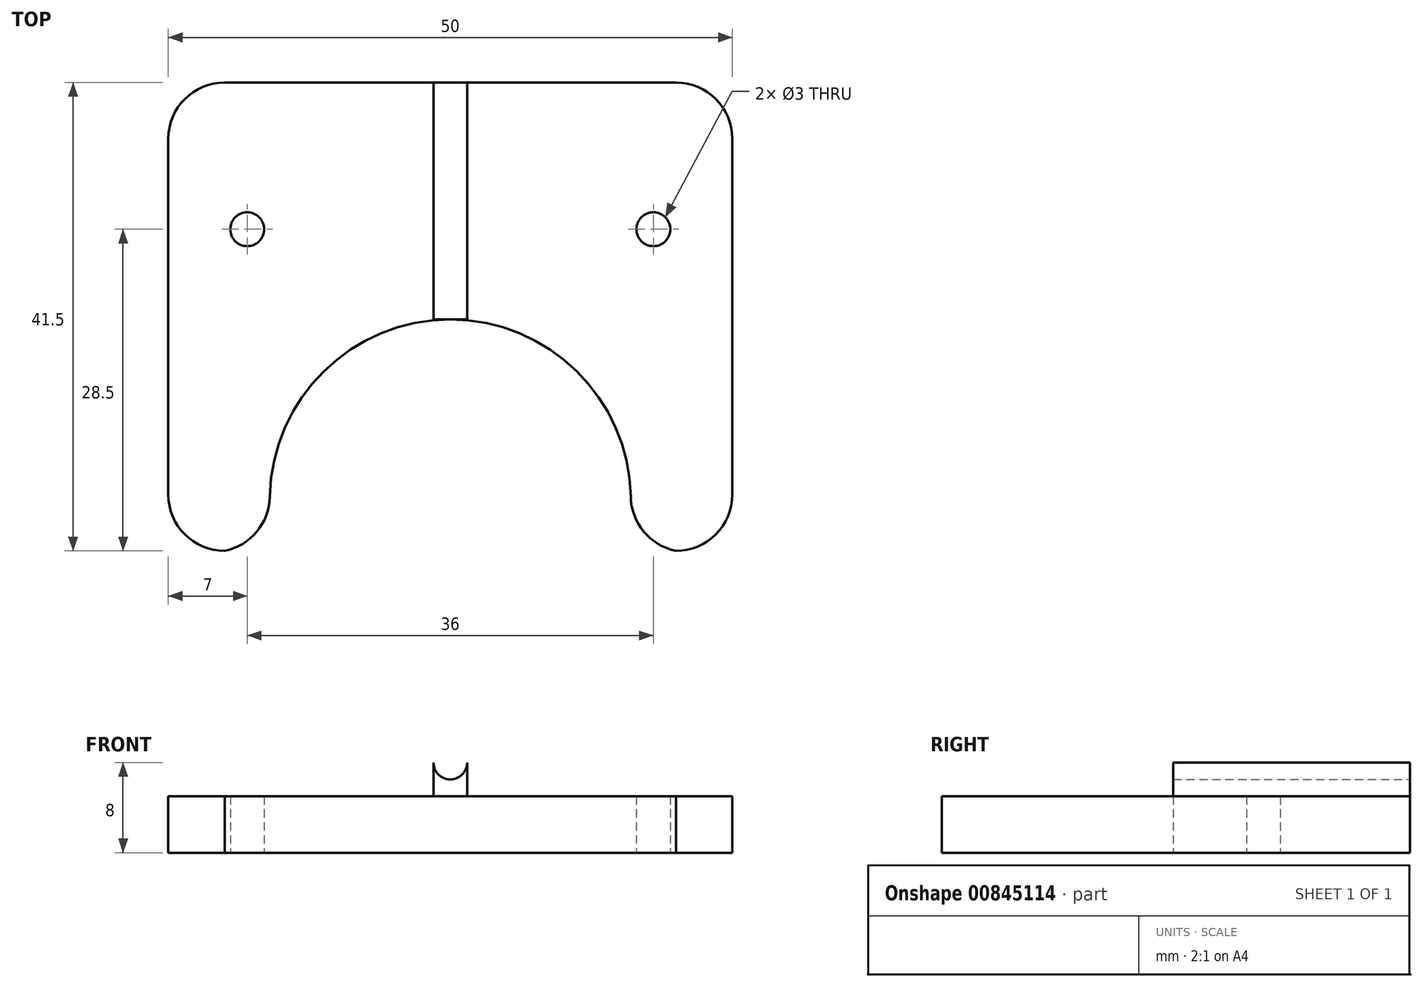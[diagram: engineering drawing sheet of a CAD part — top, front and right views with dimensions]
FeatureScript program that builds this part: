
annotation { "Feature Type Name" : "Feature", "Feature Type Description" : "" }
export const myFeature = defineFeature(function(context is Context, id is Id, definition is map)
    precondition{}
    {
        {
            var Q0;
            Q0=qCreatedBy(makeId("Top.planeOp"),FACE);
            var sketch = newSketch(context, id + "F0", { "sketchPlane" : qUnion([Q0])});
            skLineSegment(sketch, "E0.bottom", {"start": v(25, -10.5) * mm, "end": v(-25, -10.5) * mm});
            skLineSegment(sketch, "E0.top", {"start": v(25, 10.5) * mm, "end": v(-25, 10.5) * mm});
            skLineSegment(sketch, "E0.left", {"start": v(25, -10.5) * mm, "end": v(25, 10.5) * mm});
            skLineSegment(sketch, "E0.right", {"start": v(-25, -10.5) * mm, "end": v(-25, 10.5) * mm});
            skPoint(sketch, "E0.middle", {"position": v(0, 0) * mm});
            skCircle(sketch, "E1", {"center": v(-18, -2.5) * mm, "radius": 1.5 * mm});
            skCircle(sketch, "E2", {"center": v(18, -2.5) * mm, "radius": 1.5 * mm});
            skCircle(sketch, "E3", {"center": v(0, -26.5) * mm, "radius": 17 * mm, "construction": true});
            skCircle(sketch, "E4", {"center": v(0, -26.5) * mm, "radius": 16 * mm});
            skLineSegment(sketch, "E5.bottom", {"start": v(-25, -10.5) * mm, "end": v(25, -10.5) * mm});
            skLineSegment(sketch, "E5.top", {"start": v(-25, -40.5) * mm, "end": v(25, -40.5) * mm});
            skLineSegment(sketch, "E5.left", {"start": v(-25, -10.5) * mm, "end": v(-25, -40.5) * mm});
            skLineSegment(sketch, "E5.right", {"start": v(25, -10.5) * mm, "end": v(25, -40.5) * mm});
            skLineSegment(sketch, "E6", {"start": v(0, -26.5) * mm, "end": v(-16, -26.5) * mm});
            skLineSegment(sketch, "E7", {"start": v(0.62, -26.5) * mm, "end": v(16, -26.5) * mm});
            skLineSegment(sketch, "E8", {"start": v(-16, -26.5) * mm, "end": v(-16, -40.5) * mm});
            skLineSegment(sketch, "E9", {"start": v(16, -26.5) * mm, "end": v(16, -40.5) * mm});
            skLineSegment(sketch, "E10", {"start": v(-25, -31) * mm, "end": v(25, -31) * mm});
            skSolve(sketch);
        }
        {
            var Q0;
            Q0=makeQuery(id+"F0.imprint","IMPRINT",FACE,{"disambiguationData":[TD([[makeQuery(id+"F0.imprint","IMPRINT",EDGE,{"derivedFrom":sQuery(id+"F0.wireOp",EDGE,"E0.top")}),1.0]])]});
            var Q1;
            {var subQ5=sQuery(id+"F0.wireOp",EDGE,"E4");var subQ7=sQuery(id+"F0.wireOp",EDGE,"E9");var subQ8=makeQuery(id+"F0.imprint","INTERSECT",VERTEX,{"derivedFrom":[subQ5,subQ7]});Q1=makeQuery(id+"F0.imprint","IMPRINT",FACE,{"disambiguationData":[TD([[makeQuery(id+"F0.imprint","IMPRINT",EDGE,{"disambiguationData":[TD([[subQ8,-1.0]])],"derivedFrom":subQ5}),-1.0]])]});}
            var Q2;
            {var subQ0=sQuery(id+"F0.wireOp",EDGE,"E8");var subQ1=sQuery(id+"F0.wireOp",EDGE,"E4");var subQ2=makeQuery(id+"F0.imprint","INTERSECT",VERTEX,{"derivedFrom":[subQ1,subQ0]});Q2=makeQuery(id+"F0.imprint","IMPRINT",FACE,{"disambiguationData":[TD([[makeQuery(id+"F0.imprint","IMPRINT",EDGE,{"disambiguationData":[TD([[subQ2,1.0]])],"derivedFrom":subQ1}),-1.0]])]});}
            extrude(context, id + "F1", {"entities" : qUnion([Q0, Q1, Q2]), "depth" : 5 * mm, "offsetDistance" : 25 * mm});
        }
        {
            var Q0;
            Q0=makeQuery(id+"F1.opExtrude","SWEPT_EDGE",EDGE,{"disambiguationData":[OSD([sQuery(id+"F0.wireOp",EDGE,"E5.right"),sQuery(id+"F0.wireOp",EDGE,"E10")])]});
            var Q1;
            Q1=makeQuery(id+"F1.opExtrude","SWEPT_EDGE",EDGE,{"disambiguationData":[OSD([sQuery(id+"F0.wireOp",EDGE,"E5.left"),sQuery(id+"F0.wireOp",EDGE,"E10")])]});
            var Q2;
            Q2=makeQuery(id+"F1.opExtrude","SWEPT_EDGE",EDGE,{"disambiguationData":[OSD([sQuery(id+"F0.wireOp",EDGE,"E0.top"),sQuery(id+"F0.wireOp",EDGE,"E0.right")])]});
            var Q3;
            Q3=makeQuery(id+"F1.opExtrude","SWEPT_EDGE",EDGE,{"disambiguationData":[OSD([sQuery(id+"F0.wireOp",EDGE,"E0.top"),sQuery(id+"F0.wireOp",EDGE,"E0.left")])]});
            fillet(context, id + "F2", {"entities" : qUnion([Q0, Q1, Q2, Q3]), "radius" : 5 * mm, "tangentPropagation" : true, "allowEdgeOverflow" : false});
        }
        {
            var Q0;
            Q0=makeQuery(id+"F1.opExtrude","CAP_FACE",FACE,{"disambiguationData":[OSD([sQuery(id+"F0.wireOp",EDGE,"E0.top"),sQuery(id+"F0.wireOp",EDGE,"E0.left"),sQuery(id+"F0.wireOp",EDGE,"E0.right"),sQuery(id+"F0.wireOp",EDGE,"E1"),sQuery(id+"F0.wireOp",EDGE,"E2"),sQuery(id+"F0.wireOp",EDGE,"E4"),sQuery(id+"F0.wireOp",EDGE,"E5.left"),sQuery(id+"F0.wireOp",EDGE,"E5.right"),sQuery(id+"F0.wireOp",EDGE,"E8"),sQuery(id+"F0.wireOp",EDGE,"E9"),sQuery(id+"F0.wireOp",EDGE,"E10")])],"isStart":false});
            var sketch = newSketch(context, id + "F3", { "sketchPlane" : qUnion([Q0])});
            skLineSegment(sketch, "E11.bottom", {"start": v(1.5, 10.5) * mm, "end": v(-1.5, 10.5) * mm});
            skLineSegment(sketch, "E11.top", {"start": v(1.5, -10.5) * mm, "end": v(-1.5, -10.5) * mm});
            skLineSegment(sketch, "E11.left", {"start": v(1.5, 10.5) * mm, "end": v(1.5, -10.5) * mm});
            skLineSegment(sketch, "E11.right", {"start": v(-1.5, 10.5) * mm, "end": v(-1.5, -10.5) * mm});
            skPoint(sketch, "E11.middle", {"position": v(0, 0) * mm});
            skSolve(sketch);
        }
        {
            var Q0;
            Q0 = qSketchRegion(id + "F3", true);
            extrude(context, id + "F4", {"entities" : qUnion([Q0]), "operationType" : NewBodyOperationType.ADD, "depth" : 3 * mm, "offsetDistance" : 25 * mm});
        }
        {
            var Q0;
            Q0=makeQuery(id+"F4.boolean.opBoolean","MERGE",FACE,{"derivedFrom":[makeQuery(id+"F1.opExtrude","SWEPT_FACE",FACE,{"disambiguationData":[OSD([sQuery(id+"F0.wireOp",EDGE,"E0.top")])]}),makeQuery(id+"F4.opExtrude","SWEPT_FACE",FACE,{"disambiguationData":[OSD([sQuery(id+"F3.wireOp",EDGE,"E11.bottom")])]})]});
            var sketch = newSketch(context, id + "F5", { "sketchPlane" : qUnion([Q0])});
            skCircle(sketch, "E12", {"center": v(0, 8) * mm, "radius": 1.5 * mm});
            skSolve(sketch);
        }
        {
            var Q0;
            Q0 = qSketchRegion(id + "F5", true);
            extrude(context, id + "F6", {"entities" : qUnion([Q0]), "operationType" : NewBodyOperationType.REMOVE, "endBound" : BoundingType.UP_TO_NEXT, "oppositeDirection" : true, "depth" : 25 * mm, "offsetDistance" : 25 * mm});
        }
        {
            var Q0;
            Q0=makeQuery(id+"F1.opExtrude","SWEPT_EDGE",EDGE,{"disambiguationData":[OSD([sQuery(id+"F0.wireOp",EDGE,"E9"),sQuery(id+"F0.wireOp",EDGE,"E10")])]});
            var Q1;
            Q1=makeQuery(id+"F1.opExtrude","SWEPT_EDGE",EDGE,{"disambiguationData":[OSD([sQuery(id+"F0.wireOp",EDGE,"E8"),sQuery(id+"F0.wireOp",EDGE,"E10")])]});
            fillet(context, id + "F7", {"entities" : qUnion([Q0, Q1]), "radius" : 5 * mm, "tangentPropagation" : true, "allowEdgeOverflow" : false});
        }
    });
